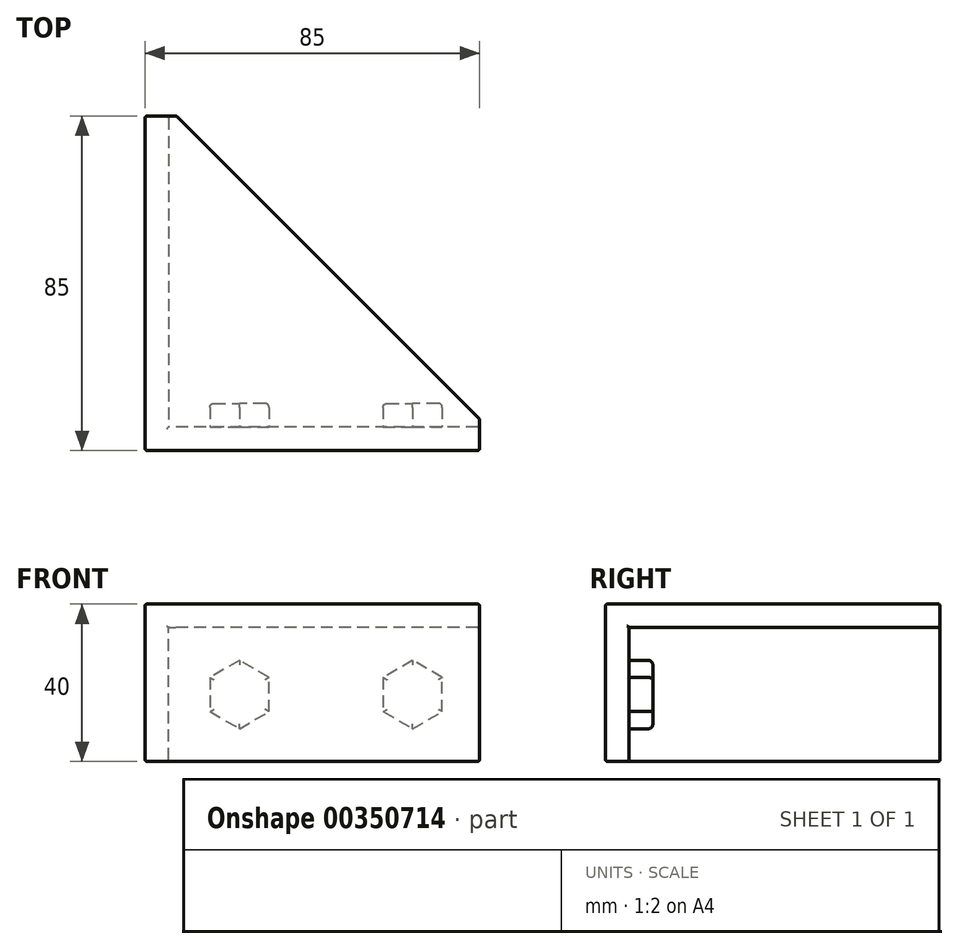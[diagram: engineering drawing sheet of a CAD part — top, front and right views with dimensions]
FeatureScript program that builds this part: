
annotation { "Feature Type Name" : "Feature", "Feature Type Description" : "" }
export const myFeature = defineFeature(function(context is Context, id is Id, definition is map)
    precondition{}
    {
        {
            var Q0;
            Q0=qCreatedBy(makeId("Top.planeOp"),FACE);
            var sketch = newSketch(context, id + "F0", { "sketchPlane" : qUnion([Q0])});
            skLineSegment(sketch, "E0", {"start": v(0, 0) * mm, "end": v(0, 85) * mm});
            skLineSegment(sketch, "E1", {"start": v(0, 85) * mm, "end": v(8, 85) * mm});
            skLineSegment(sketch, "E2", {"start": v(0, 0) * mm, "end": v(85, 0) * mm});
            skLineSegment(sketch, "E3", {"start": v(85, 0) * mm, "end": v(85, 8) * mm});
            skLineSegment(sketch, "E4", {"start": v(85, 8) * mm, "end": v(8, 85) * mm});
            skSolve(sketch);
        }
        {
            var Q0;
            Q0 = qSketchRegion(id + "F0", true);
            extrude(context, id + "F1", {"entities" : qUnion([Q0]), "depth" : 6 * mm});
        }
        {
            var Q0;
            Q0=qCreatedBy(makeId("Top.planeOp"),FACE);
            var sketch = newSketch(context, id + "F2", { "sketchPlane" : qUnion([Q0])});
            skLineSegment(sketch, "E5", {"start": v(0, 0) * mm, "end": v(85, 0) * mm});
            skLineSegment(sketch, "E6", {"start": v(85, 0) * mm, "end": v(85, 6) * mm});
            skLineSegment(sketch, "E7", {"start": v(0, 85) * mm, "end": v(6, 85) * mm});
            skLineSegment(sketch, "E8", {"start": v(6, 85) * mm, "end": v(6, 6) * mm});
            skLineSegment(sketch, "E9", {"start": v(85, 6) * mm, "end": v(6, 6) * mm});
            skLineSegment(sketch, "E10", {"start": v(0, 85) * mm, "end": v(0, 0) * mm});
            skSolve(sketch);
        }
        {
            var Q0;
            Q0=makeQuery(id+"F2.imprint","IMPRINT",FACE,{"disambiguationData":[TD([[makeQuery(id+"F2.imprint","IMPRINT",EDGE,{"derivedFrom":sQuery(id+"F2.wireOp",EDGE,"E5")}),1.0]])]});
            extrude(context, id + "F3", {"entities" : qUnion([Q0]), "operationType" : NewBodyOperationType.ADD, "oppositeDirection" : true, "depth" : 34 * mm});
        }
        {
            var Q0;
            Q0=makeQuery(id+"F3.opExtrude","CAP_FACE",FACE,{"disambiguationData":[OSD([sQuery(id+"F2.wireOp",EDGE,"E5"),sQuery(id+"F2.wireOp",EDGE,"E6"),sQuery(id+"F2.wireOp",EDGE,"E7"),sQuery(id+"F2.wireOp",EDGE,"E8"),sQuery(id+"F2.wireOp",EDGE,"E9"),sQuery(id+"F2.wireOp",EDGE,"E10")])],"isStart":false});
            var Q1;
            Q1=makeQuery(id+"F3.boolean.opBoolean","MERGE",FACE,{"derivedFrom":[makeQuery(id+"F1.opExtrude","SWEPT_FACE",FACE,{"disambiguationData":[OSD([sQuery(id+"F0.wireOp",EDGE,"E0")])]}),makeQuery(id+"F3.opExtrude","SWEPT_FACE",FACE,{"disambiguationData":[OSD([sQuery(id+"F2.wireOp",EDGE,"E10")])]})]});
            var Q2;
            Q2=makeQuery(id+"F3.boolean.opBoolean","MERGE",FACE,{"derivedFrom":[makeQuery(id+"F1.opExtrude","SWEPT_FACE",FACE,{"disambiguationData":[OSD([sQuery(id+"F0.wireOp",EDGE,"E1")])]}),makeQuery(id+"F3.opExtrude","SWEPT_FACE",FACE,{"disambiguationData":[OSD([sQuery(id+"F2.wireOp",EDGE,"E7")])]})]});
            var Q3;
            Q3=makeQuery(id+"F1.opExtrude","SWEPT_FACE",FACE,{"disambiguationData":[OSD([sQuery(id+"F0.wireOp",EDGE,"E4")])]});
            var Q4;
            Q4=makeQuery(id+"F1.opExtrude","CAP_FACE",FACE,{"disambiguationData":[OSD([sQuery(id+"F0.wireOp",EDGE,"E0"),sQuery(id+"F0.wireOp",EDGE,"E1"),sQuery(id+"F0.wireOp",EDGE,"E2"),sQuery(id+"F0.wireOp",EDGE,"E3"),sQuery(id+"F0.wireOp",EDGE,"E4")])],"isStart":false});
            var Q5;
            Q5=makeQuery(id+"F3.boolean.opBoolean","MERGE",FACE,{"derivedFrom":[makeQuery(id+"F1.opExtrude","SWEPT_FACE",FACE,{"disambiguationData":[OSD([sQuery(id+"F0.wireOp",EDGE,"E2")])]}),makeQuery(id+"F3.opExtrude","SWEPT_FACE",FACE,{"disambiguationData":[OSD([sQuery(id+"F2.wireOp",EDGE,"E5")])]})]});
            var Q6;
            Q6=makeQuery(id+"F3.boolean.opBoolean","MERGE",FACE,{"derivedFrom":[makeQuery(id+"F1.opExtrude","SWEPT_FACE",FACE,{"disambiguationData":[OSD([sQuery(id+"F0.wireOp",EDGE,"E3")])]}),makeQuery(id+"F3.opExtrude","SWEPT_FACE",FACE,{"disambiguationData":[OSD([sQuery(id+"F2.wireOp",EDGE,"E6")])]})]});
            fillet(context, id + "F4", {"entities" : qUnion([Q0, Q1, Q2, Q3, Q4, Q5, Q6]), "radius" : .5 * mm, "tangentPropagation" : true, "allowEdgeOverflow" : false});
        }
        {
            var Q0;
            Q0=makeQuery(id+"F3.opExtrude","SWEPT_EDGE",EDGE,{"disambiguationData":[OSD([sQuery(id+"F2.wireOp",EDGE,"E8"),sQuery(id+"F2.wireOp",EDGE,"E9")])]});
            cPlane(context, id + "F5", {"entities" : qUnion([Q0]), "cplaneType" : CPlaneType.LINE_ANGLE, "offset" : 25 * mm, "angle" : 45 * degree, "oppositeDirection" : true, "width" : 150 * mm, "height" : 150 * mm});
        }
        {
            var Q0;
            Q0=makeQuery(id+"F3.opExtrude","SWEPT_FACE",FACE,{"disambiguationData":[OSD([sQuery(id+"F2.wireOp",EDGE,"E9")])]});
            var sketch = newSketch(context, id + "F6", { "sketchPlane" : qUnion([Q0])});
            skCircle(sketch, "E11.cCircle", {"center": v(-68, -17) * mm, "radius": 7.5 * mm, "construction": true});
            skLineSegment(sketch, "E11.0", {"start": v(-60.5, -21.33) * mm, "end": v(-68, -25.66) * mm});
            skLineSegment(sketch, "E11.1", {"start": v(-68, -25.66) * mm, "end": v(-75.5, -21.33) * mm});
            skLineSegment(sketch, "E11.2", {"start": v(-75.5, -21.33) * mm, "end": v(-75.5, -12.67) * mm});
            skLineSegment(sketch, "E11.3", {"start": v(-75.5, -12.67) * mm, "end": v(-68, -8.34) * mm});
            skLineSegment(sketch, "E11.4", {"start": v(-68, -8.34) * mm, "end": v(-60.5, -12.67) * mm});
            skLineSegment(sketch, "E11.5", {"start": v(-60.5, -12.67) * mm, "end": v(-60.5, -21.33) * mm});
            skPoint(sketch, "E11.0.midPoint", {"position": v(-64.25, -23.5) * mm});
            skCircle(sketch, "E12.cCircle", {"center": v(-24, -17) * mm, "radius": 7.5 * mm, "construction": true});
            skLineSegment(sketch, "E12.0", {"start": v(-16.5, -21.33) * mm, "end": v(-24, -25.66) * mm});
            skLineSegment(sketch, "E12.1", {"start": v(-24, -25.66) * mm, "end": v(-31.5, -21.33) * mm});
            skLineSegment(sketch, "E12.2", {"start": v(-31.5, -21.33) * mm, "end": v(-31.5, -12.67) * mm});
            skLineSegment(sketch, "E12.3", {"start": v(-31.5, -12.67) * mm, "end": v(-24, -8.34) * mm});
            skLineSegment(sketch, "E12.4", {"start": v(-24, -8.34) * mm, "end": v(-16.5, -12.67) * mm});
            skLineSegment(sketch, "E12.5", {"start": v(-16.5, -12.67) * mm, "end": v(-16.5, -21.33) * mm});
            skPoint(sketch, "E12.0.midPoint", {"position": v(-20.25, -23.5) * mm});
            skSolve(sketch);
        }
        {
            var Q0;
            Q0 = qSketchRegion(id + "F6", true);
            extrude(context, id + "F7", {"entities" : qUnion([Q0]), "operationType" : NewBodyOperationType.ADD, "depth" : 6 * mm});
        }
        {
            var Q0;
            Q0=makeQuery(id+"F7.opExtrude","CAP_FACE",FACE,{"disambiguationData":[OSD([sQuery(id+"F6.wireOp",EDGE,"E11.0"),sQuery(id+"F6.wireOp",EDGE,"E11.1"),sQuery(id+"F6.wireOp",EDGE,"E11.2"),sQuery(id+"F6.wireOp",EDGE,"E11.3"),sQuery(id+"F6.wireOp",EDGE,"E11.4"),sQuery(id+"F6.wireOp",EDGE,"E11.5")])],"isStart":false});
            var Q1;
            Q1=makeQuery(id+"F7.opExtrude","CAP_FACE",FACE,{"disambiguationData":[OSD([sQuery(id+"F6.wireOp",EDGE,"E12.0"),sQuery(id+"F6.wireOp",EDGE,"E12.1"),sQuery(id+"F6.wireOp",EDGE,"E12.2"),sQuery(id+"F6.wireOp",EDGE,"E12.3"),sQuery(id+"F6.wireOp",EDGE,"E12.4"),sQuery(id+"F6.wireOp",EDGE,"E12.5")])],"isStart":false});
            var Q2;
            Q2=makeQuery(id+"F2U1PAq30QkQj9L_1.1.F7.opExtrude","CAP_FACE",FACE,{"disambiguationData":[OSD([sQuery(id+"F6.wireOp",EDGE,"E12.0"),sQuery(id+"F6.wireOp",EDGE,"E12.1"),sQuery(id+"F6.wireOp",EDGE,"E12.2"),sQuery(id+"F6.wireOp",EDGE,"E12.3"),sQuery(id+"F6.wireOp",EDGE,"E12.4"),sQuery(id+"F6.wireOp",EDGE,"E12.5")])],"isStart":false});
            var Q3;
            Q3=makeQuery(id+"F2U1PAq30QkQj9L_1.1.F7.opExtrude","CAP_FACE",FACE,{"disambiguationData":[OSD([sQuery(id+"F6.wireOp",EDGE,"E11.0"),sQuery(id+"F6.wireOp",EDGE,"E11.1"),sQuery(id+"F6.wireOp",EDGE,"E11.2"),sQuery(id+"F6.wireOp",EDGE,"E11.3"),sQuery(id+"F6.wireOp",EDGE,"E11.4"),sQuery(id+"F6.wireOp",EDGE,"E11.5")])],"isStart":false});
            fillet(context, id + "F8", {"entities" : qUnion([Q0, Q1, Q2, Q3]), "radius" : 1 * mm, "tangentPropagation" : true, "allowEdgeOverflow" : false});
        }
    });
